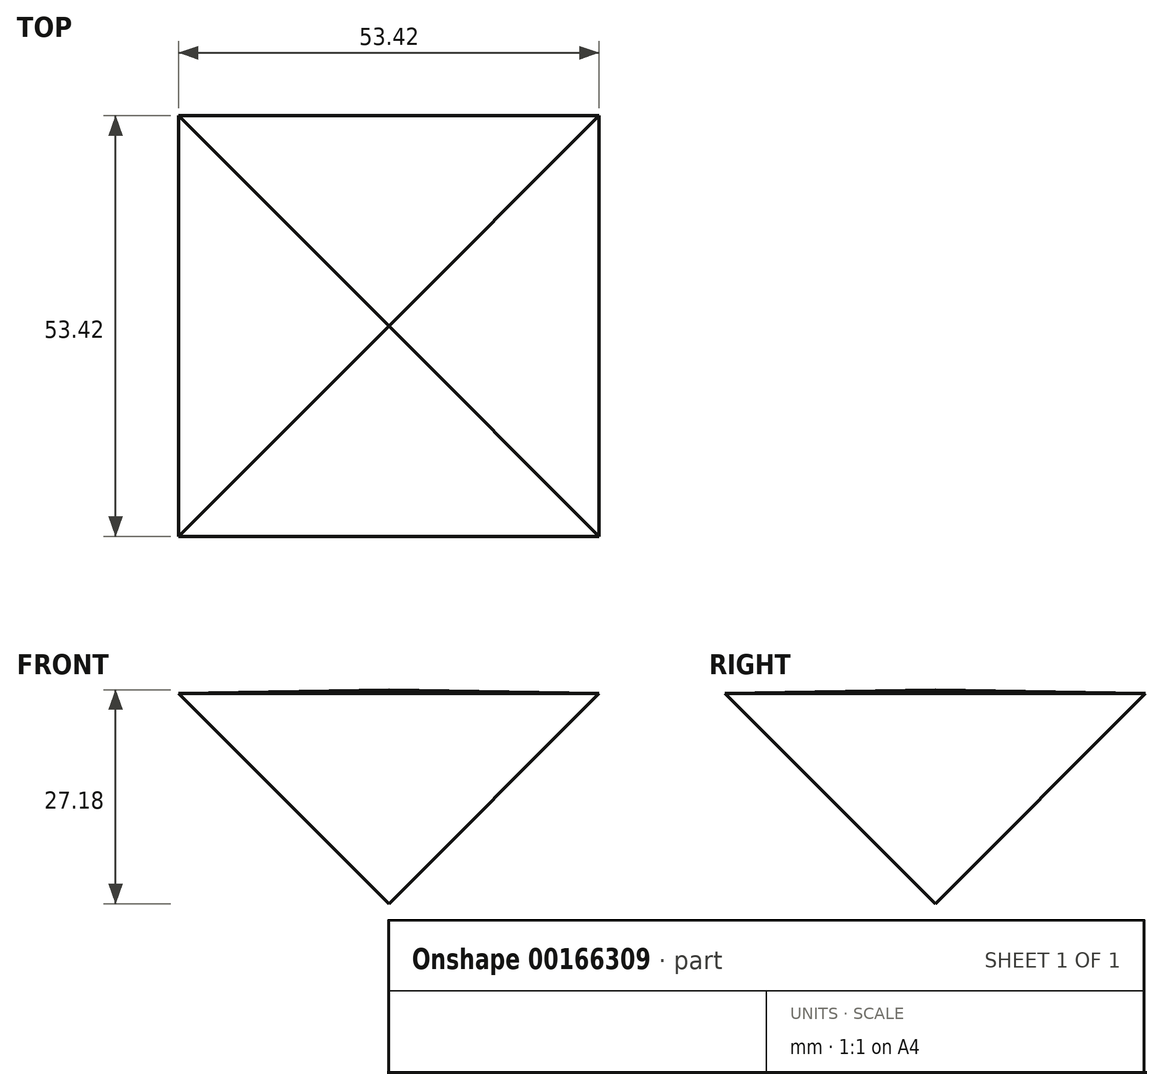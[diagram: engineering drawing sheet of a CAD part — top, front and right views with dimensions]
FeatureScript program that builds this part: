
annotation { "Feature Type Name" : "Feature", "Feature Type Description" : "" }
export const myFeature = defineFeature(function(context is Context, id is Id, definition is map)
    precondition{}
    {
        {
            var Q0;
            Q0=qCreatedBy(makeId("Top.planeOp"),FACE);
            var sketch = newSketch(context, id + "F0", { "sketchPlane" : qUnion([Q0])});
            skLineSegment(sketch, "E0.bottom", {"start": v(26.7, 26.7) * mm, "end": v(-26.7, 26.7) * mm});
            skLineSegment(sketch, "E0.top", {"start": v(26.7, -26.7) * mm, "end": v(-26.7, -26.7) * mm});
            skLineSegment(sketch, "E0.left", {"start": v(26.7, 26.7) * mm, "end": v(26.7, -26.7) * mm});
            skLineSegment(sketch, "E0.right", {"start": v(-26.7, 26.7) * mm, "end": v(-26.7, -26.7) * mm});
            skPoint(sketch, "E0.middle", {"position": v(0, 0) * mm});
            skSolve(sketch);
        }
        {
            var Q0;
            Q0=makeQuery(id+"F0.imprint","IMPRINT",FACE,{"disambiguationData":[TD([[makeQuery(id+"F0.imprint","IMPRINT",EDGE,{"derivedFrom":sQuery(id+"F0.wireOp",EDGE,"E0.bottom")}),1.0]])]});
            extrude(context, id + "F1", {"entities" : qUnion([Q0]), "depth" : 254 * mm, "hasDraft" : true, "draftAngle" : 89 * degree, "draftPullDirection" : true, "hasSecondDirection" : true, "secondDirectionOppositeDirection" : true, "secondDirectionDepth" : 254 * mm, "hasSecondDirectionDraft" : true, "secondDirectionDraftAngle" : 45 * degree, "secondDirectionDraftPullDirection" : true});
        }
    });
